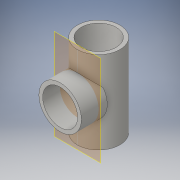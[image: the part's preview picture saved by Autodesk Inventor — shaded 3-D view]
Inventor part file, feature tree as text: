
AUTODESK INVENTOR PART (.ipt)
format: ipt  version: 2016 (Build 200138000, 138)  size: 142,336 bytes
history: native  units: in
note: dims shown in document units (in); Inventor stores cm internally (conversion verified against a paired STEP export)
features: extrude x3, sketch x3, plane x1
ambient origin geometry x8: Origin, YZ Plane, XZ Plane, XY Plane, X Axis, Y Axis, Z Axis, Center Point
bodies: Solid1 (feature_tree)
feature tree (7):
  extrude  "Extrusion1"  Depth=1.315in
  plane  "Work Plane1"
  extrude  "Extrusion2"  Depth=1.315in
  extrude  "Extrusion3"  Depth=0.65in TaperAngle=0.0deg
  sketch  "Sketch1"  dims[d0=1.6in d1=1.315in]
  sketch  "Sketch2"  dims[d2=3.112in d3=0.0in d4=1.315in]
  sketch  "Sketch3"  dims[d5=1.6in d6=0.65in d7=0.325in d8=0.0in d9=0.0in d10=1.315in d11=1.0in d12=0.0in]
